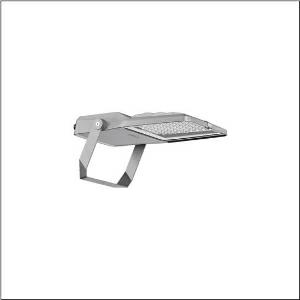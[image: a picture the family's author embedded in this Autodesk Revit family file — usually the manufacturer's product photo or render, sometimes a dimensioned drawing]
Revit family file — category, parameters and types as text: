
# Revit family: floodlight_fl_21_iq_mini___pl43_5xa7772b1a1a_21a9
name_source: partatom
category: Lighting Fixtures
units: mm (PartAtom-declared; Revit-internal decimal feet)

## family parameters
Cut with Voids When Loaded = No
Host = Face
Light Source = No
Part Type = Normal
Room Calculation Point = No
Round Connector Dimension = Use Diameter
Shared = No

## types (1)
- --- (1 x LED, 5300 lm, 45.5 W, 2200K)
    Apparent Load = 46 VA
    CIE Flux Codes = 27 78 99 100 100
    Color Rendering = 70
    Color Temperature = 2200K
    Default Elevation = 1800 mm
    Description = Floodlight FL 21 iQ mini, floodlight, primary light control with lens, of PMMA, primary optical cover: protective disc, of toughened safety glass, transparent, light distribution: PL43, light emission: direct distribution, installation type: surface-mounted, LED, High Power LED, rated luminous flux: 5.300lm, luminous efficacy: 117lm/W, light colour: 722, colour temperature: 2200K, control gear: iQ Street-Remote/DALI, control: Street-Remote, Auto-Match, Temp-Guard, Night-Set, Smart-Wire, Desk-Remote (wireless, voltage-free reading and setting of iQ features in the workshop via application-optimized NFC function/RFID function), optimised constant luminous flux control (CLO 2.0), with terminal, 6-pole, mains connection: 220..240V, AC, 50/60Hz, start of lifetime: 46W, end of service life: 48W, reduction: 21W, luminaire housing, of diecast aluminium, powder-coated, Siteco® metallic grey (DB 702S), corrosivity category C5 mid according to DIN EN ISO 12944, suitable for swimming pools, chlorine-resistant, sealing non-destructively replaceable, mounting bracket, of steel, galvanised, powder-coated, Siteco® metallic grey (DB 702S), protection rating (complete): IP66, insulation class (complete): insulation class II (safety insulation), certification: CE, ENEC, VDE, protection symbol: D, impact resistance: IK08, permissible operating ambient temperature: -40..+40°C, permissible operating ambient temperature for outdoor applications: -40..+50°C, standard: DIN EN 12944, LABS conformity tested according to VDMA 24364:2018-05, packaging unit: 1 piece

Light Distribution: PL43
    Height = 70 mm
    Lamp = 1 x LED
    Lamp Light Flux = 5300 lm
    Lamp Power = 45.5 W
    Lamp count = 1
    Length = 485 mm
    Luminous efficacy = 116 lm/W
    Manufacturer = Siteco
    ModVariant = No
    Model = 5XA7772B1A1A
    Number of Poles = 1
    OnlyDefault = Yes
    Power Factor = 1
    Product Name = Floodlight FL 21 iQ mini | PL43
    Product group = floodlight | pylon annexe
    ProductGroupID = 6201
    Protection Class = Protection class II
    Protection Degree = IP 66
    RLX_Detail_Level = 1
    RLX_Emergency_Light_Flux = 0 lm
    RLX_Emergency_Type = 0
    RLX_Emergency_Type_DB = No
    RlxData = <blob elided: 96085 chars, md5=7ba724a6>
    Socket = socket
    Standby Power = 0 W
    System Light Flux = 5300 lm
    System Power = 46 W
    Type Comments = factory setting: luminous flux: 100 % | dim-lin: 254 | 463 mA
    Type Image = l_1006845.jpg
    URL = http://relux.com
    VarID = @adj_184311
    Voltage = 0 V
    Weight = 0.00 kg
    Width = 337 mm

## geometry (parser evidence)
native form markers: Blend x4, Sweep x12
no freeform markers — native parametric forms only
